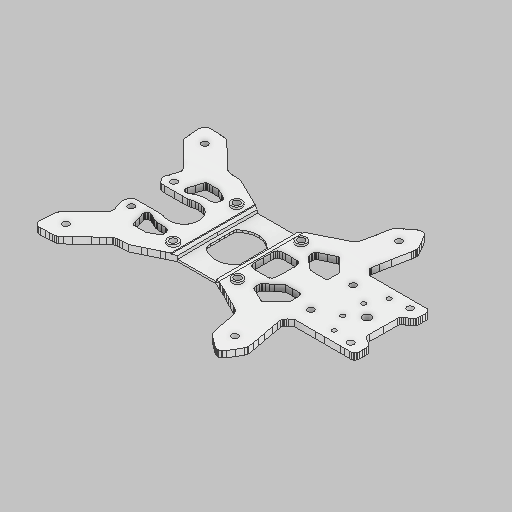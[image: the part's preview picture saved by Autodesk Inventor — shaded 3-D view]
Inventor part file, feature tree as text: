
AUTODESK INVENTOR PART (.ipt)
format: ipt  version: 2025.2 (Build 292293000, 293)  size: 3,017,728 bytes
history: native  units: in
note: dims shown in document units (in); Inventor stores cm internally (conversion verified against a paired STEP export)
features: extrude x17, sketch x17
ambient origin geometry x8: Origin, YZ Plane, XZ Plane, XY Plane, X Axis, Y Axis, Z Axis, Center Point
bodies: Solid1 (feature_tree)
feature tree (34):
  extrude  "Extrusion1"  Depth=0.1181in
  extrude  "Extrusion2"  Depth=0.1181in
  extrude  "Extrusion3"  Depth=0.126in
  extrude  "Extrusion4"  Depth=1.2008in
  extrude  "Extrusion5"  Depth=1.2008in
  extrude  "Extrusion6"  Depth=0.6004in
  extrude  "Extrusion7"  TaperAngle=90.0deg  [1 undecoded]
  extrude  "Extrusion8"  Depth=0.6004in
  extrude  "Extrusion9"  Depth=0.1181in TaperAngle=0.0deg
  extrude  "Extrusion10"  Depth=0.1181in
  extrude  "Extrusion11"  Depth=0.1181in TaperAngle=0.0deg
  extrude  "Extrusion12"  Depth=0.1181in
  extrude  "Extrusion13"  Depth=0.1969in
  extrude  "Extrusion14"  Depth=0.1181in TaperAngle=0.0deg
  extrude  "Extrusion15"  Depth=0.151in
  extrude  "Extrusion16"  Depth=0.1181in
  extrude  "Extrusion22"  Depth=0.1181in
  sketch  "Sketch1"  dims[d0=0.1181in d1=0.0in d2=5.1217in]
  sketch  "Sketch2"  dims[d3=0.1181in d4=0.0in d5=0.126in]
  sketch  "Sketch3"  dims[d6=0.126in d7=0.126in]
  sketch  "Sketch4"  dims[d8=0.126in d9=1.2008in]
  sketch  "Sketch5"  dims[d10=1.2008in d11=1.2008in]
  sketch  "Sketch6"  dims[d12=1.2008in d13=0.6004in]
  sketch  "Sketch7"  dims[d14=0.6004in d17=90.0deg]
  sketch  "Sketch8"  dims[d18=0.6004in d19=0.6004in]
  sketch  "Sketch9"  dims[d20=0.6004in d21=0.1181in d22=0.0in]
  sketch  "Sketch10"  dims[d23=0.1181in d24=0.1181in]
  sketch  "Sketch11"  dims[d25=0.1181in d26=0.1181in d27=0.0in]
  sketch  "Sketch12"  dims[d29=0.1181in d30=0.0in d31=0.1181in]
  sketch  "Sketch13"  dims[d32=0.1969in d33=0.1969in]
  sketch  "Sketch14"  dims[d34=0.1181in d35=0.0in d36=0.1181in d37=0.0in]
  sketch  "Sketch15"  dims[d38=0.1554in d39=0.151in]
  sketch  "Sketch17"  dims[d40=0.1181in d41=0.0in d42=0.1181in]
  sketch  "Sketch23"  dims[d43=0.1181in d44=0.1181in d45=0.1181in d46=0.5512in d47=0.5512in d48=0.3937in d49=0.3937in d50=0.9013in d51=0.1181in d52=0.0in d53=0.1181in d54=0.0in d55=0.1575in d56=0.1181in d57=0.0in d58=0.1181in d59=0.0in d60=0.0827in d61=0.1969in d62=0.5512in d63=0.0827in d64=0.315in d65=0.1575in d66=0.1181in d67=0.0in d68=0.1969in d69=0.1969in d70=0.1969in d71=0.1969in d72=0.0394in d73=0.0in d74=0.7874in d75=0.4528in d76=1.5748in d77=0.9055in d78=0.0197in d79=0.0in d80=0.0787in d81=0.0787in d82=0.0591in d83=0.0in d100=0.0197in d101=0.0in d90=0.0197in d91=0.0344in d92=0.0197in d93=0.0344in]
note: 1 required parameter value undecoded (feature->parameter linkage not recoverable at this tier; creation-order binding heuristic only, values carry confidence <= 0.55)
